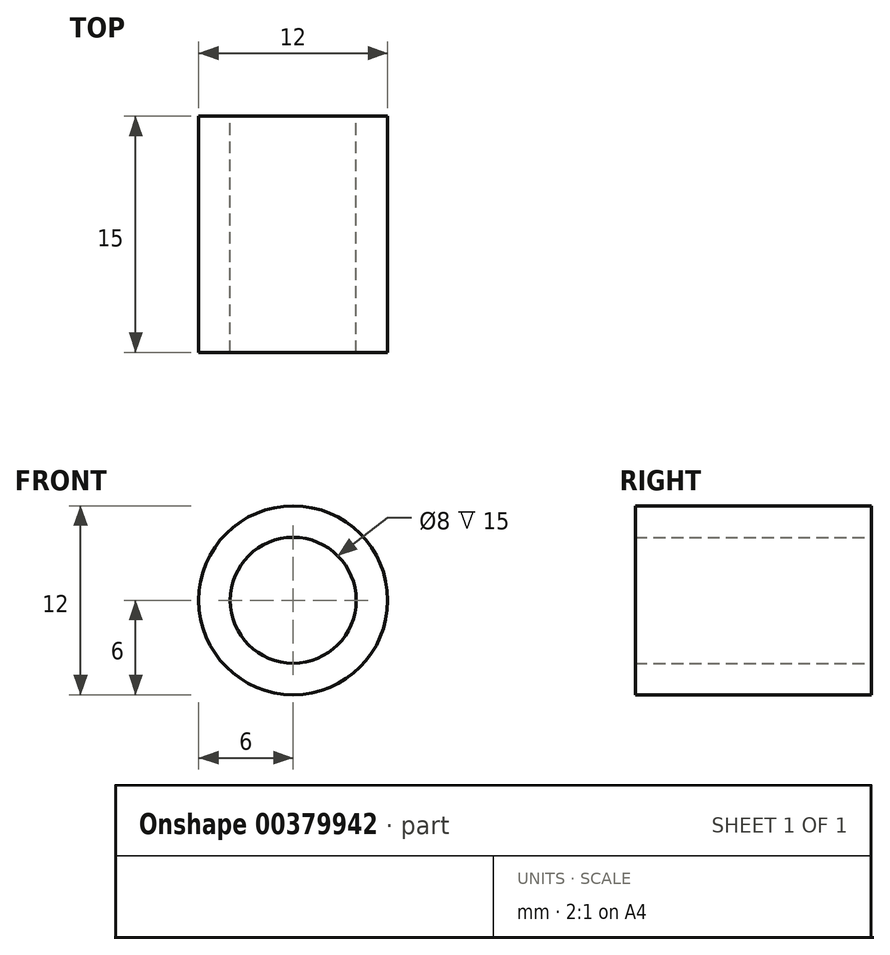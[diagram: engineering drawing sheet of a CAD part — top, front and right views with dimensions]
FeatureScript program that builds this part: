
annotation { "Feature Type Name" : "Feature", "Feature Type Description" : "" }
export const myFeature = defineFeature(function(context is Context, id is Id, definition is map)
    precondition{}
    {
        {
            var Q0;
            Q0=qCreatedBy(makeId("Front.planeOp"),FACE);
            var sketch = newSketch(context, id + "F0", { "sketchPlane" : qUnion([Q0])});
            skCircle(sketch, "E0", {"center": v(0, 0) * mm, "radius": 6 * mm});
            skCircle(sketch, "E1", {"center": v(0, 0) * mm, "radius": 4 * mm});
            skSolve(sketch);
        }
        {
            var Q0;
            Q0 = qSketchRegion(id + "F0", true);
            extrude(context, id + "F1", {"entities" : qUnion([Q0]), "depth" : 15 * mm});
        }
    });
